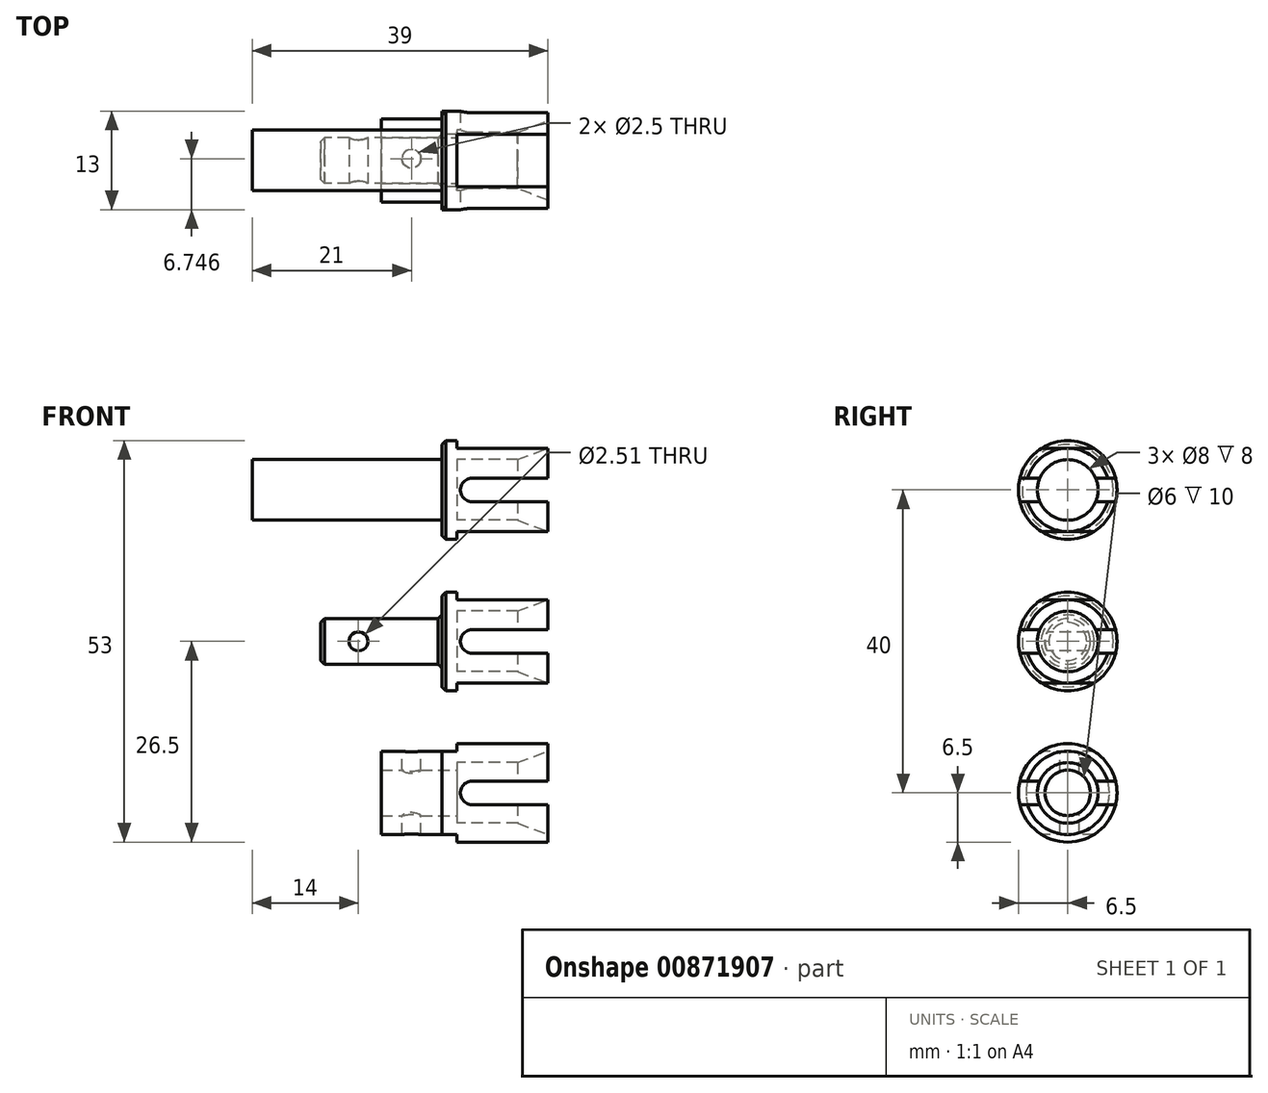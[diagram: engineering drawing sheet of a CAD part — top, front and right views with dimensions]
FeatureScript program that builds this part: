
annotation { "Feature Type Name" : "Feature", "Feature Type Description" : "" }
export const myFeature = defineFeature(function(context is Context, id is Id, definition is map)
    precondition{}
    {
        {
            var Q0;
            Q0=qCreatedBy(makeId("Front.planeOp"),FACE);
            var sketch = newSketch(context, id + "F0", { "sketchPlane" : qUnion([Q0])});
            skLineSegment(sketch, "E0", {"start": v(0, 0) * mm, "end": v(0, 5.7) * mm, "construction": true});
            skLineSegment(sketch, "E1", {"start": v(0, 0) * mm, "end": v(14.57, 0) * mm, "construction": true});
            skLineSegment(sketch, "E2", {"start": v(11, 4) * mm, "end": v(11, 6.5) * mm});
            skLineSegment(sketch, "E3", {"start": v(11, 6.5) * mm, "end": v(-3, 6.5) * mm});
            skLineSegment(sketch, "E4", {"start": v(-3, 6.5) * mm, "end": v(-3, 3) * mm});
            skLineSegment(sketch, "E5", {"start": v(-3, 3) * mm, "end": v(-19, 3) * mm});
            skLineSegment(sketch, "E6", {"start": v(-19, 3) * mm, "end": v(-19, 0) * mm});
            skLineSegment(sketch, "E7", {"start": v(-19, 0) * mm, "end": v(-1, 0) * mm});
            skLineSegment(sketch, "E8", {"start": v(-1, 0) * mm, "end": v(-1, 4) * mm});
            skLineSegment(sketch, "E9", {"start": v(-1, 4) * mm, "end": v(11, 4) * mm});
            skSolve(sketch);
        }
        {
            var Q0;
            Q0=makeQuery(id+"F0.imprint","IMPRINT",FACE,{"disambiguationData":[TD([[makeQuery(id+"F0.imprint","IMPRINT",EDGE,{"derivedFrom":sQuery(id+"F0.wireOp",EDGE,"E2")}),1.0]])]});
            var Q1;
            Q1=sQuery(id+"F0.wireOp",EDGE,"E1");
            revolve(context, id + "F1", {"surfaceOperationType" : NewSurfaceOperationType.NEW, "entities" : qUnion([Q0]), "axis" : qUnion([Q1]), "revolveType" : RevolveType.FULL});
        }
        {
            var Q0;
            Q0=qCreatedBy(makeId("Front.planeOp"),FACE);
            var sketch = newSketch(context, id + "F2", { "sketchPlane" : qUnion([Q0])});
            skLineSegment(sketch, "E10", {"start": v(1, 0) * mm, "end": v(11, 0) * mm, "construction": true});
            skArc(sketch, "E11.0.startCap", {"start": v(1, -1.55) * mm, "mid": v(-0.55, 0) * mm, "end": v(1, 1.55) * mm});
            skArc(sketch, "E11.0.endCap", {"start": v(11, 1.55) * mm, "mid": v(12.55, 0) * mm, "end": v(11, -1.55) * mm});
            skLineSegment(sketch, "E11.0.left", {"start": v(1, 1.55) * mm, "end": v(11, 1.55) * mm});
            skLineSegment(sketch, "E11.0.right", {"start": v(1, -1.55) * mm, "end": v(11, -1.55) * mm});
            skCircle(sketch, "E12", {"center": v(-14, 0) * mm, "radius": 1.25 * mm});
            skSolve(sketch);
        }
        {
            var Q0;
            Q0=makeQuery(id+"F1.opRevolve","SWEPT_EDGE",EDGE,{"disambiguationData":[OSD([sQuery(id+"F0.wireOp",EDGE,"E2"),sQuery(id+"F0.wireOp",EDGE,"E9")])]});
            chamfer(context, id + "F3", {"entities" : qUnion([Q0]), "chamferType" : ChamferType.TWO_OFFSETS, "width1" : 1.5 * mm, "oppositeDirection" : false, "width2" : 4 * mm, "tangentPropagation" : true});
        }
        {
            var Q0;
            Q0=qSketchRegion(id+"F2",true);
            extrude(context, id + "F4", {"entities" : qUnion([Q0]), "operationType" : NewBodyOperationType.REMOVE, "oppositeDirection" : true, "depth" : 25 * mm, "offsetDistance" : 25 * mm, "symmetric" : true});
        }
        {
            var Q0;
            Q0=qCreatedBy(makeId("Front.planeOp"),FACE);
            var sketch = newSketch(context, id + "F5", { "sketchPlane" : qUnion([Q0])});
            skLineSegment(sketch, "E13", {"start": v(-3, 6.5) * mm, "end": v(11, 6.5) * mm, "construction": true});
            skLineSegment(sketch, "E14", {"start": v(11, -6.5) * mm, "end": v(-3, -6.5) * mm, "construction": true});
            skLineSegment(sketch, "E15.bottom", {"start": v(11, -6.5) * mm, "end": v(-1, -6.5) * mm});
            skLineSegment(sketch, "E15.top", {"start": v(11, -5.5) * mm, "end": v(-1, -5.5) * mm});
            skLineSegment(sketch, "E15.left", {"start": v(11, -6.5) * mm, "end": v(11, -5.5) * mm});
            skLineSegment(sketch, "E15.right", {"start": v(-1, -6.5) * mm, "end": v(-1, -5.5) * mm});
            skLineSegment(sketch, "E16.bottom", {"start": v(11, 6.5) * mm, "end": v(-1, 6.5) * mm});
            skLineSegment(sketch, "E16.top", {"start": v(11, 5.5) * mm, "end": v(-1, 5.5) * mm});
            skLineSegment(sketch, "E16.left", {"start": v(11, 6.5) * mm, "end": v(11, 5.5) * mm});
            skLineSegment(sketch, "E16.right", {"start": v(-1, 6.5) * mm, "end": v(-1, 5.5) * mm});
            skLineSegment(sketch, "E17", {"start": v(0, 0) * mm, "end": v(13.93, 0) * mm, "construction": true});
            skSolve(sketch);
        }
        {
            var Q0;
            Q0=makeQuery(id+"F1.opRevolve","SWEPT_BODY",BODY,{"disambiguationData":[OSD([sQuery(id+"F0.wireOp",EDGE,"E2"),sQuery(id+"F0.wireOp",EDGE,"E3"),sQuery(id+"F0.wireOp",EDGE,"E4"),sQuery(id+"F0.wireOp",EDGE,"E5"),sQuery(id+"F0.wireOp",EDGE,"E6"),sQuery(id+"F0.wireOp",EDGE,"E7"),sQuery(id+"F0.wireOp",EDGE,"E8"),sQuery(id+"F0.wireOp",EDGE,"E9")])]});
            transform(context, id + "F6", {"entities" : qUnion([Q0]), "transformType" : TransformType.TRANSLATION_3D, "dx" : 0 * mm, "dy" : 0 * mm, "dz" : -20 * mm, "makeCopy" : true});
        }
        {
            var Q0;
            Q0=qSketchRegion(id+"F5",true);
            extrude(context, id + "F7", {"entities" : qUnion([Q0]), "operationType" : NewBodyOperationType.REMOVE, "oppositeDirection" : true, "depth" : 25 * mm, "offsetDistance" : 25 * mm, "symmetric" : true});
        }
        {
            var Q0;
            Q0=makeQuery(id+"F1.opRevolve","SWEPT_EDGE",EDGE,{"disambiguationData":[OSD([sQuery(id+"F0.wireOp",EDGE,"E5"),sQuery(id+"F0.wireOp",EDGE,"E6")])]});
            var Q1;
            Q1=makeQuery(id+"F1.opRevolve","SWEPT_EDGE",EDGE,{"disambiguationData":[OSD([sQuery(id+"F0.wireOp",EDGE,"E3"),sQuery(id+"F0.wireOp",EDGE,"E4")])]});
            chamfer(context, id + "F8", {"entities" : qUnion([Q0, Q1]), "width" : 0.5 * mm, "tangentPropagation" : true});
        }
        {
            var Q0;
            Q0=makeQuery(id+"F1.opRevolve","SWEPT_EDGE",EDGE,{"disambiguationData":[OSD([sQuery(id+"F0.wireOp",EDGE,"E4"),sQuery(id+"F0.wireOp",EDGE,"E5")])]});
            chamfer(context, id + "F9", {"entities" : qUnion([Q0]), "width" : 0.5 * mm, "tangentPropagation" : true});
        }
        {
            var Q0;
            Q0=makeQuery(id+"F6.opPattern","COPY",FACE,{"derivedFrom":makeQuery(id+"F1.opRevolve","SWEPT_FACE",FACE,{"disambiguationData":[OSD([sQuery(id+"F0.wireOp",EDGE,"E6")])]}),"instanceName":"1"});
            var Q1;
            Q1=makeQuery(id+"F6.opPattern","COPY",FACE,{"derivedFrom":makeQuery(id+"F1.opRevolve","SWEPT_FACE",FACE,{"disambiguationData":[OSD([sQuery(id+"F0.wireOp",EDGE,"E4")])]}),"instanceName":"1"});
            extrude(context, id + "F10", {"entities" : qUnion([Q0]), "operationType" : NewBodyOperationType.REMOVE, "endBound" : BoundingType.UP_TO_SURFACE, "oppositeDirection" : true, "depth" : 25 * mm, "endBoundEntityFace" : qUnion([Q1]), "offsetDistance" : 25 * mm});
        }
        {
            var Q0;
            {var subQ0=sQuery(id+"F0.wireOp",EDGE,"E4");Q0=makeQuery(id+"F10.boolean.opBoolean","MERGE",FACE,{"derivedFrom":[makeQuery(id+"F6.opPattern","COPY",FACE,{"derivedFrom":makeQuery(id+"F1.opRevolve","SWEPT_FACE",FACE,{"disambiguationData":[OSD([subQ0])]}),"instanceName":"1"}),makeQuery(id+"F10.opExtrude","CAP_FACE",FACE,{"disambiguationData":[OSD([subQ0])],"isStart":false})]});}
            extrude(context, id + "F11", {"entities" : qUnion([Q0]), "operationType" : NewBodyOperationType.ADD, "depth" : 8 * mm, "offsetDistance" : 25 * mm});
        }
        {
            var Q0;
            Q0=makeQuery(id+"F11.opExtrude","CAP_FACE",FACE,{"disambiguationData":[OSD([sQuery(id+"F0.wireOp",EDGE,"E4")])],"isStart":false});
            var sketch = newSketch(context, id + "F12", { "sketchPlane" : qUnion([Q0])});
            skPoint(sketch, "E18", {"position": v(0, -20) * mm});
            skSolve(sketch);
        }
        {
            var Q0;
            Q0=sQuery(id+"F12.wireOp",VERTEX,"E18");
            var Q1;
            Q1=makeQuery(id+"F6.opPattern","COPY",BODY,{"derivedFrom":makeQuery(id+"F1.opRevolve","SWEPT_BODY",BODY,{"disambiguationData":[OSD([sQuery(id+"F0.wireOp",EDGE,"E2"),sQuery(id+"F0.wireOp",EDGE,"E3"),sQuery(id+"F0.wireOp",EDGE,"E4"),sQuery(id+"F0.wireOp",EDGE,"E5"),sQuery(id+"F0.wireOp",EDGE,"E6"),sQuery(id+"F0.wireOp",EDGE,"E7"),sQuery(id+"F0.wireOp",EDGE,"E8"),sQuery(id+"F0.wireOp",EDGE,"E9")])]}),"instanceName":"1"});
            hole(context, id + "F13", {"style" : HoleStyle.SIMPLE, "endStyle" : HoleEndStyle.THROUGH, "holeDiameter" : 6 * mm, "majorDiameter" : 5 * mm, "isTappedThrough" : true, "tappedDepth" : 12 * mm, "tapClearance" : 3, "locations" : qUnion([Q0]), "scope" : qUnion([Q1])});
        }
        {
            var Q0;
            Q0=makeQuery(id+"F11.opExtrude","CAP_FACE",FACE,{"disambiguationData":[OSD([sQuery(id+"F0.wireOp",EDGE,"E4")])],"isStart":false});
            var sketch = newSketch(context, id + "F14", { "sketchPlane" : qUnion([Q0])});
            skCircle(sketch, "E19", {"center": v(0, -20) * mm, "radius": 5.5 * mm});
            skCircle(sketch, "E20", {"center": v(0, -20) * mm, "radius": 6.5 * mm});
            skSolve(sketch);
        }
        {
            var Q0;
            Q0=qSketchRegion(id+"F14",true);
            extrude(context, id + "F15", {"entities" : qUnion([Q0]), "operationType" : NewBodyOperationType.REMOVE, "oppositeDirection" : true, "depth" : 8 * mm, "offsetDistance" : 25 * mm});
        }
        {
            var Q0;
            Q0=qCreatedBy(makeId("Top.planeOp"),FACE);
            cPlane(context, id + "F16", {"entities" : qUnion([Q0]), "cplaneType" : CPlaneType.OFFSET, "offset" : 20 * mm, "oppositeDirection" : true, "width" : 150 * mm, "height" : 150 * mm});
        }
        {
            var Q0;
            Q0=qCreatedBy(id+"F16.planeOp",FACE);
            var sketch = newSketch(context, id + "F17", { "sketchPlane" : qUnion([Q0])});
            skCircle(sketch, "E21", {"center": v(-7, 0.25) * mm, "radius": 1.25 * mm});
            skSolve(sketch);
        }
        {
            var Q0;
            Q0=qCreatedBy(makeId("Front.planeOp"),FACE);
            var sketch = newSketch(context, id + "F18", { "sketchPlane" : qUnion([Q0])});
            skLineSegment(sketch, "E22", {"start": v(-11, -14.5) * mm, "end": v(-3, -14.5) * mm, "construction": true});
            skLineSegment(sketch, "E23.0", {"start": v(-3, -26.5) * mm, "end": v(-3, -13.5) * mm, "construction": true});
            skLineSegment(sketch, "E24.bottom", {"start": v(-3, -14.5) * mm, "end": v(-1, -14.5) * mm});
            skLineSegment(sketch, "E24.top", {"start": v(-3, -13.5) * mm, "end": v(-1, -13.5) * mm});
            skLineSegment(sketch, "E24.left", {"start": v(-3, -14.5) * mm, "end": v(-3, -13.5) * mm});
            skLineSegment(sketch, "E24.right", {"start": v(-1, -14.5) * mm, "end": v(-1, -13.5) * mm});
            skLineSegment(sketch, "E25", {"start": v(-3, -25.5) * mm, "end": v(-11, -25.5) * mm, "construction": true});
            skLineSegment(sketch, "E26.bottom", {"start": v(-3, -25.5) * mm, "end": v(-1, -25.5) * mm});
            skLineSegment(sketch, "E26.top", {"start": v(-3, -26.5) * mm, "end": v(-1, -26.5) * mm});
            skLineSegment(sketch, "E26.left", {"start": v(-3, -25.5) * mm, "end": v(-3, -26.5) * mm});
            skLineSegment(sketch, "E26.right", {"start": v(-1, -25.5) * mm, "end": v(-1, -26.5) * mm});
            skSolve(sketch);
        }
        {
            var Q0;
            Q0=qSketchRegion(id+"F18",true);
            extrude(context, id + "F19", {"entities" : qUnion([Q0]), "operationType" : NewBodyOperationType.REMOVE, "oppositeDirection" : true, "depth" : 25 * mm, "offsetDistance" : 25 * mm, "symmetric" : true});
        }
        {
            var Q0;
            Q0=qSketchRegion(id+"F17",true);
            extrude(context, id + "F20", {"entities" : qUnion([Q0]), "operationType" : NewBodyOperationType.REMOVE, "oppositeDirection" : true, "depth" : 25 * mm, "offsetDistance" : 25 * mm, "symmetric" : true});
        }
        {
            var Q0;
            Q0=makeQuery(id+"F1.opRevolve","SWEPT_BODY",BODY,{"disambiguationData":[OSD([sQuery(id+"F0.wireOp",EDGE,"E2"),sQuery(id+"F0.wireOp",EDGE,"E3"),sQuery(id+"F0.wireOp",EDGE,"E4"),sQuery(id+"F0.wireOp",EDGE,"E5"),sQuery(id+"F0.wireOp",EDGE,"E6"),sQuery(id+"F0.wireOp",EDGE,"E7"),sQuery(id+"F0.wireOp",EDGE,"E8"),sQuery(id+"F0.wireOp",EDGE,"E9")])]});
            transform(context, id + "F21", {"entities" : qUnion([Q0]), "transformType" : TransformType.TRANSLATION_3D, "dx" : 0 * mm, "dy" : 0 * mm, "dz" : 20 * mm, "makeCopy" : true});
        }
        {
            var Q0;
            Q0=makeQuery(id+"F21.opPattern","COPY",FACE,{"derivedFrom":makeQuery(id+"F1.opRevolve","SWEPT_FACE",FACE,{"disambiguationData":[OSD([sQuery(id+"F0.wireOp",EDGE,"E4")])]}),"instanceName":"1"});
            var sketch = newSketch(context, id + "F22", { "sketchPlane" : qUnion([Q0])});
            skCircle(sketch, "E27", {"center": v(0, 20) * mm, "radius": 4 * mm});
            skSolve(sketch);
        }
        {
            var Q0;
            Q0=qSketchRegion(id+"F22",true);
            extrude(context, id + "F23", {"entities" : qUnion([Q0]), "operationType" : NewBodyOperationType.ADD, "depth" : 25 * mm, "offsetDistance" : 25 * mm});
        }
    });
